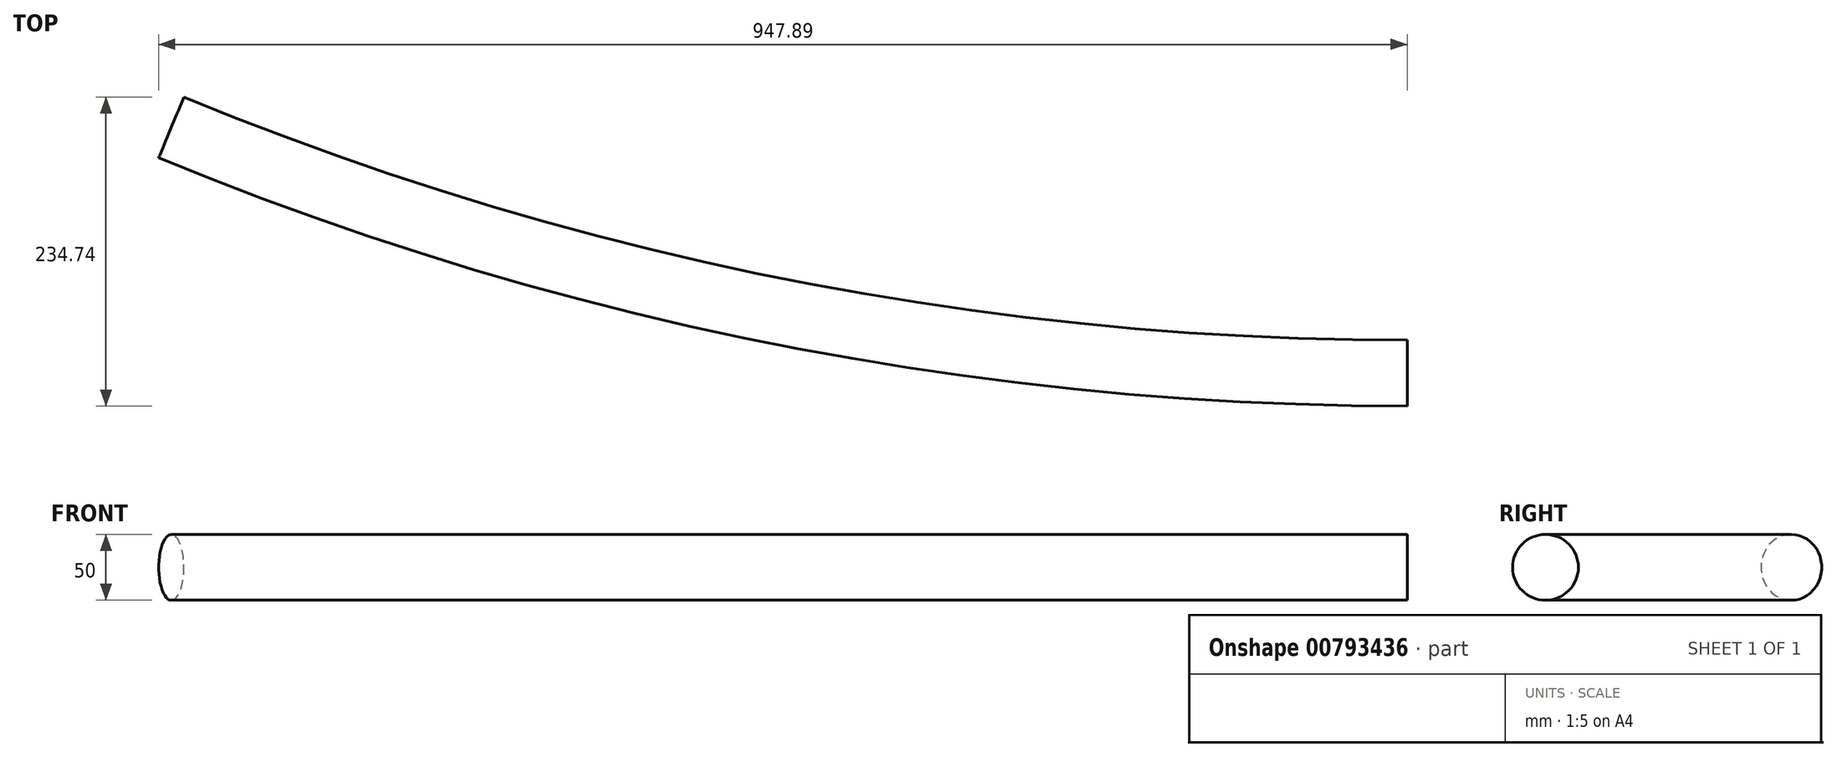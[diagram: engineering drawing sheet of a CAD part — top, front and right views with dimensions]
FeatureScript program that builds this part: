
annotation { "Feature Type Name" : "Feature", "Feature Type Description" : "" }
export const myFeature = defineFeature(function(context is Context, id is Id, definition is map)
    precondition{}
    {
        {
            var Q0;
            Q0=qCreatedBy(makeId("Top.planeOp"),FACE);
            var sketch = newSketch(context, id + "F0", { "sketchPlane" : qUnion([Q0])});
            skPoint(sketch, "E0.orphan", {"position": v(17967.28, 0) * mm});
            skPoint(sketch, "E1.orphan", {"position": v(0, 4126.94) * mm});
            skPoint(sketch, "E2.orphan", {"position": v(4126.94, 0) * mm});
            skArc(sketch, "E3", {"start": v(-956.7, -2309.7) * mm, "mid": v(-487.73, -2451.96) * mm, "end": v(0, -2500) * mm});
            skPoint(sketch, "E4.end.orphan", {"position": v(-956.7, -2309.7) * mm});
            skSolve(sketch);
        }
        {
            var Q0;
            Q0=qCreatedBy(makeId("Right.planeOp"),FACE);
            var sketch = newSketch(context, id + "F1", { "sketchPlane" : qUnion([Q0])});
            skCircle(sketch, "E5", {"center": v(-2451.96, 0) * mm, "radius": 25 * mm});
            skSolve(sketch);
        }
        {
            var Q0;
            Q0=makeQuery(id+"F1.imprint","IMPRINT",FACE,{"disambiguationData":[TD([[makeQuery(id+"F1.imprint","IMPRINT",EDGE,{"derivedFrom":sQuery(id+"F1.wireOp",EDGE,"E5")}),1.0]])]});
            var Q1;
            Q1=sQuery(id+"F0.wireOp",EDGE,"E3");
            sweep(context, id + "F2", {"profiles" : qUnion([Q0]), "path" : qUnion([Q1])});
        }
    });
